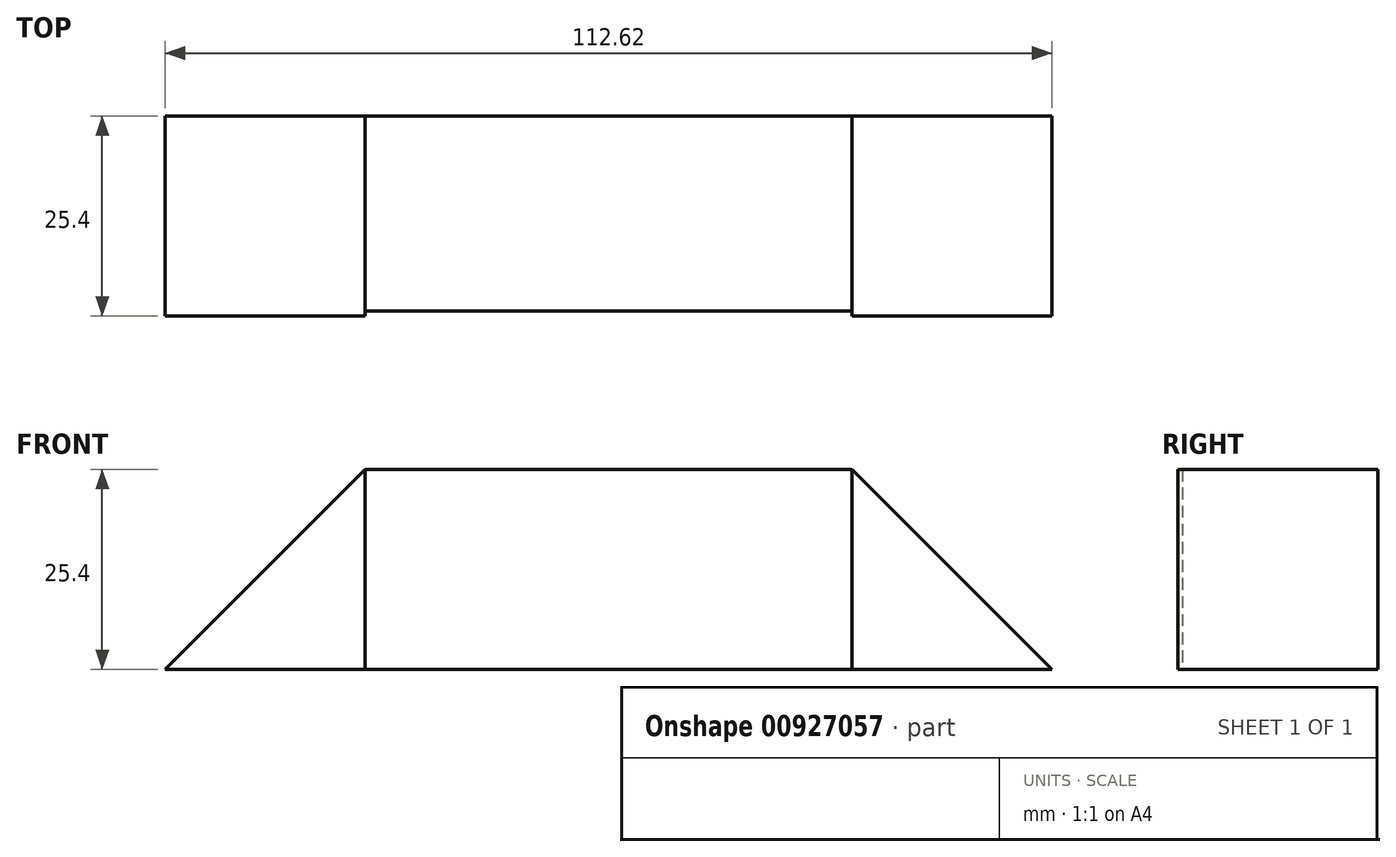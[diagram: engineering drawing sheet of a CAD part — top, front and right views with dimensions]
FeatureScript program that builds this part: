
annotation { "Feature Type Name" : "Feature", "Feature Type Description" : "" }
export const myFeature = defineFeature(function(context is Context, id is Id, definition is map)
    precondition{}
    {
        {
            var Q0;
            Q0=qCreatedBy(makeId("Top.planeOp"),FACE);
            var sketch = newSketch(context, id + "F0", { "sketchPlane" : qUnion([Q0])});
            skLineSegment(sketch, "E0.bottom", {"start": v(-30.9, 12.4) * mm, "end": v(30.9, 12.4) * mm});
            skLineSegment(sketch, "E0.top", {"start": v(-30.9, -12.4) * mm, "end": v(30.9, -12.4) * mm});
            skLineSegment(sketch, "E0.left", {"start": v(-30.9, 12.4) * mm, "end": v(-30.9, -12.4) * mm});
            skLineSegment(sketch, "E0.right", {"start": v(30.9, 12.4) * mm, "end": v(30.9, -12.4) * mm});
            skPoint(sketch, "E0.middle", {"position": v(0, 0) * mm});
            skSolve(sketch);
        }
        {
            var Q0;
            Q0=makeQuery(id+"F0.imprint","IMPRINT",FACE,{"disambiguationData":[TD([[makeQuery(id+"F0.imprint","IMPRINT",EDGE,{"derivedFrom":sQuery(id+"F0.wireOp",EDGE,"E0.bottom")}),-1.0]])]});
            extrude(context, id + "F1", {"entities" : qUnion([Q0]), "depth" : 25.4 * mm, "offsetDistance" : 25.4 * mm});
        }
        {
            var Q0;
            Q0=makeQuery(id+"F1.opExtrude","SWEPT_FACE",FACE,{"disambiguationData":[OSD([sQuery(id+"F0.wireOp",EDGE,"E0.bottom")])]});
            var sketch = newSketch(context, id + "F2", { "sketchPlane" : qUnion([Q0])});
            skLineSegment(sketch, "E1", {"start": v(-30.9, 25.4) * mm, "end": v(-56.3, 0) * mm});
            skLineSegment(sketch, "E2", {"start": v(-56.3, 0) * mm, "end": v(-30.9, 0) * mm});
            skLineSegment(sketch, "E3", {"start": v(-30.9, 0) * mm, "end": v(-30.9, 25.4) * mm});
            skLineSegment(sketch, "E4", {"start": v(30.9, 25.4) * mm, "end": v(56.3, 0) * mm});
            skLineSegment(sketch, "E5", {"start": v(56.3, 0) * mm, "end": v(30.9, 0) * mm});
            skLineSegment(sketch, "E6", {"start": v(30.9, 0) * mm, "end": v(30.9, 25.4) * mm});
            skSolve(sketch);
        }
        {
            var Q0;
            Q0=makeQuery(id+"F2.imprint","IMPRINT",FACE,{"disambiguationData":[TD([[makeQuery(id+"F2.imprint","IMPRINT",EDGE,{"derivedFrom":sQuery(id+"F2.wireOp",EDGE,"E1")}),1.0]])]});
            var Q1;
            Q1=makeQuery(id+"F2.imprint","IMPRINT",FACE,{"disambiguationData":[TD([[makeQuery(id+"F2.imprint","IMPRINT",EDGE,{"derivedFrom":sQuery(id+"F2.wireOp",EDGE,"E4")}),-1.0]])]});
            extrude(context, id + "F3", {"entities" : qUnion([Q0, Q1]), "oppositeDirection" : true, "depth" : 25.4 * mm, "offsetDistance" : 25.4 * mm});
        }
    });
